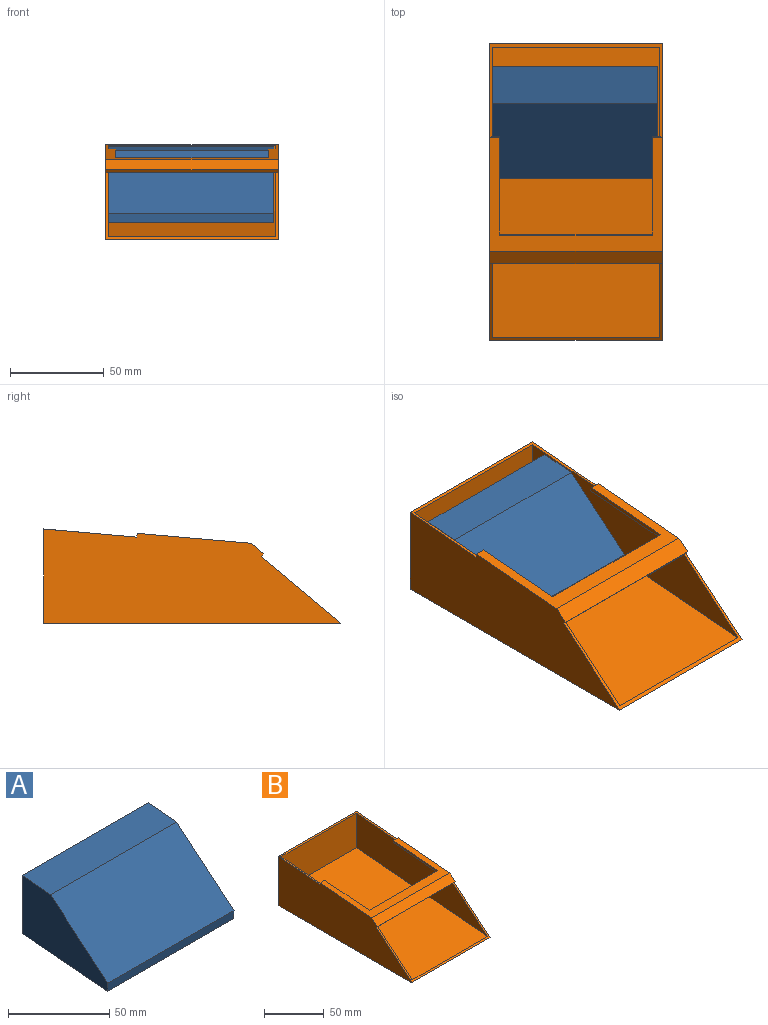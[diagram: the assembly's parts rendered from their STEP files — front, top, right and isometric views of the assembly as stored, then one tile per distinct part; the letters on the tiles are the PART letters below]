
ASSEMBLY  parts=2 mates=3
PART A: 7 faces, bbox 88x60x40.3 mm
  f0: plane 88x35.12mm, normal (0,1,0), area 3090.7mm2, adj f1,f4,f5,f6
  f1: plane 88x20mm, normal (0,-0.09,1), area 1766.7mm2, adj f0,f2,f5,f6
  f2: plane 88x40mm, normal (0,-0.64,0.77), area 4595mm2, adj f1,f3,f5,f6
  f3: plane 88x5.02mm, normal (0,-1,-0.09), area 443.4mm2, adj f2,f4,f5,f6
  f4: plane 88x59.56mm, normal (0,0.09,-1), area 5261.4mm2, adj f0,f3,f5,f6
  f5: plane 60x40.33mm, normal (1,0,0), area 1504.9mm2, adj f0,f1,f2,f3,f4
  f6: plane 60x40.33mm, normal (-1,0,0), area 1504.9mm2, adj f0,f1,f2,f3,f4
PART B: 23 faces, bbox 92x158x50.1 mm
  f0: plane 81x1.99mm, normal (0,1,0.09), area 162mm2, adj f15,f18,f19,f22
  f1: plane 92x49.64mm, normal (0,-0.09,1), area 328.2mm2, adj f4,f5,f6,f8,f9,f10,f20,f21
  f2: plane 92x42.13mm, normal (0,-0.64,0.77), area 343mm2, adj f3,f5,f6,f7,f9,f10,f16
  f3: plane 158x92mm, normal (0,0,-1), area 1337.1mm2, adj f2,f4,f5,f6,f11,f12,f13
  f4: plane 92x50.1mm, normal (0,1,0), area 3454.1mm2, adj f1,f3,f5,f6,f11,f12,f13
  f5: plane 158x50.1mm, normal (1,0,0), area 6085.9mm2, adj f1,f2,f3,f4,f16,f17,f18,f21
  f6: plane 158x50.1mm, normal (-1,0,0), area 6085.9mm2, adj f1,f2,f3,f4,f16,f17,f18,f20
  f7: plane 154.47x89mm, normal (0,-0.09,1), area 13800.2mm2, adj f2,f8,f9,f10
  f8: plane 89x35.12mm, normal (0,-1,0), area 3125.8mm2, adj f1,f7,f9,f10
  f9: plane 154.47x48.64mm, normal (1,0,0), area 4604.6mm2, adj f1,f2,f7,f8,f14,f15
  f10: plane 154.47x48.64mm, normal (-1,0,0), area 4604.6mm2, adj f1,f2,f7,f8,f14,f15
  f11: plane 148.3x89mm, normal (0,0.09,-1), area 13249.3mm2, adj f3,f4,f12,f13
  f12: plane 148.3x12.97mm, normal (1,0,0), area 962.1mm2, adj f3,f4,f11
  f13: plane 148.3x12.97mm, normal (-1,0,0), area 962.1mm2, adj f3,f4,f11
  f14: plane 89x6.13mm, normal (0,0.64,-0.77), area 712mm2, adj f9,f10,f15,f16
  f15: plane 89x60.1mm, normal (0,0.09,-1), area 1130.7mm2, adj f0,f9,f10,f14,f19,f20,f21,f22
  f16: plane 92x1.53mm, normal (0,-0.77,-0.64), area 184mm2, adj f2,f5,f6,f14,f17
  f17: plane 92x6.61mm, normal (0,-0.64,0.77), area 794mm2, adj f5,f6,f16,f18
  f18: plane 92x60.73mm, normal (0,-0.09,1), area 1369.7mm2, adj f0,f5,f6,f17,f19,f20,f21,f22
  f19: plane 52.31x6.55mm, normal (1,0,0), area 104.7mm2, adj f0,f15,f18,f20
  f20: plane 5.5x1.99mm, normal (0,1,0.09), area 11mm2, adj f1,f6,f15,f18,f19
  f21: plane 5.5x1.99mm, normal (0,1,0.09), area 11mm2, adj f1,f5,f15,f18,f22
  f22: plane 52.31x6.55mm, normal (-1,0,0), area 104.7mm2, adj f0,f15,f18,f21
PLACE A t=(-46,77.76,6.8)mm
PLACE B t=(-46,0,0)mm
MATE planar A.f4 <-> B.f7  axis (0,0.09,-1) through (-46.5,116.24,11.32)mm
MATE planar A.f5 <-> B.f10  axis (1,0,0) through (-2.5,122.7,26.45)mm
MATE parallel A.f0 <-> B.f8  axis (0,1,0) through (-46.5,146.02,31.49)mm
